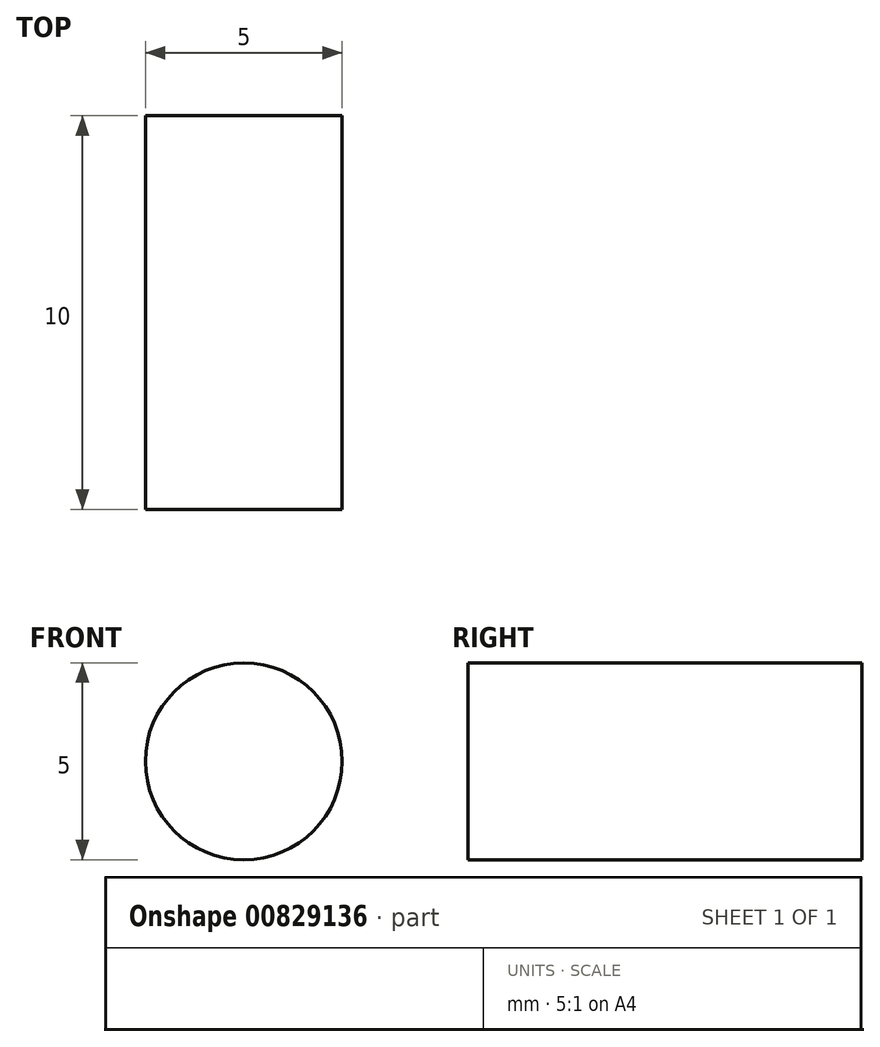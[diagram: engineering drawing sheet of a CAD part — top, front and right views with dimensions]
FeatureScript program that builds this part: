
annotation { "Feature Type Name" : "Feature", "Feature Type Description" : "" }
export const myFeature = defineFeature(function(context is Context, id is Id, definition is map)
    precondition{}
    {
        {
            var Q0;
            Q0=qCreatedBy(makeId("Front.planeOp"),FACE);
            var sketch = newSketch(context, id + "F0", { "sketchPlane" : qUnion([Q0])});
            skCircle(sketch, "E0", {"center": v(0, 0) * mm, "radius": 2.5 * mm});
            skSolve(sketch);
        }
        {
            var Q0;
            Q0 = qSketchRegion(id + "F0", true);
            extrude(context, id + "F1", {"entities" : qUnion([Q0]), "depth" : 10 * mm, "offsetDistance" : 25 * mm});
        }
    });
